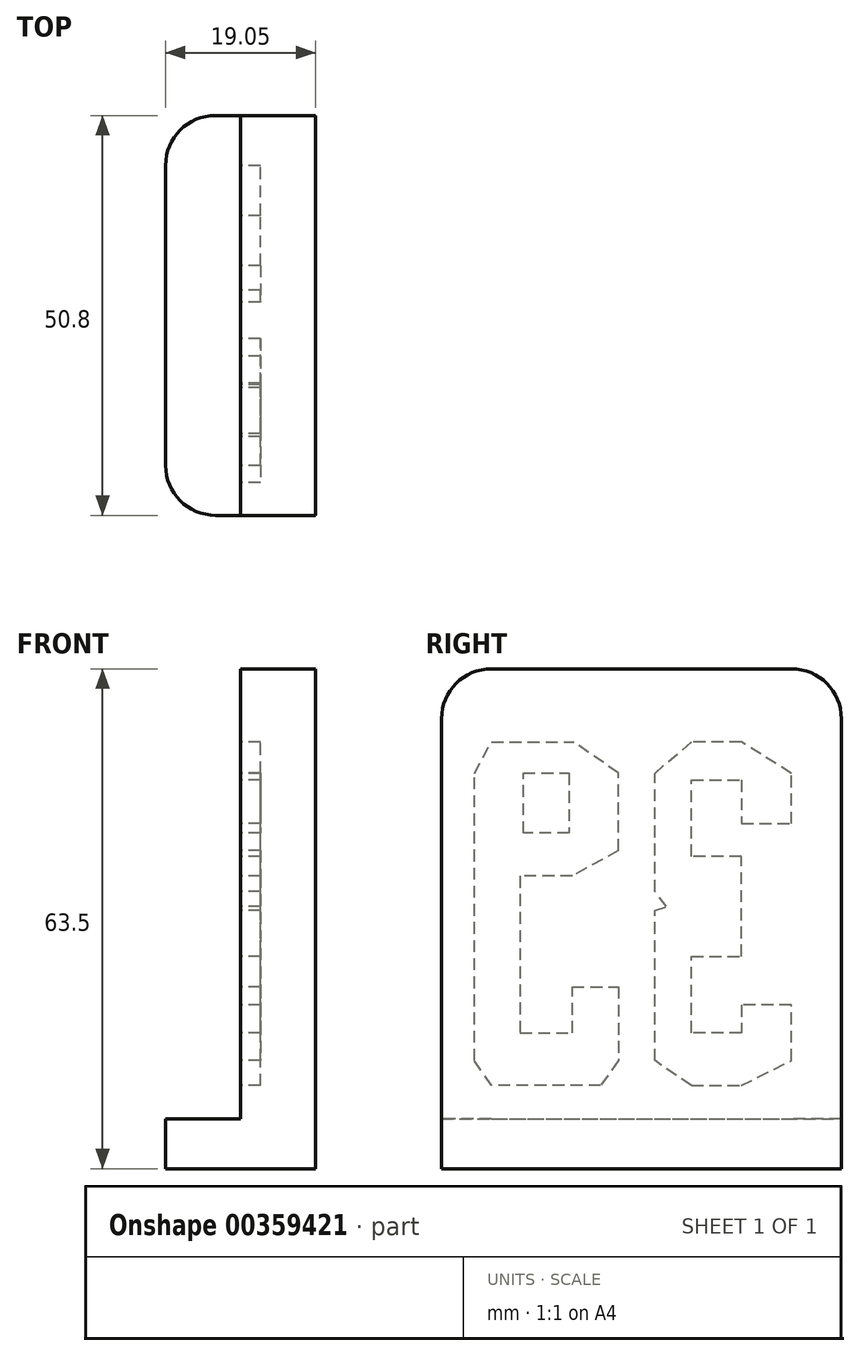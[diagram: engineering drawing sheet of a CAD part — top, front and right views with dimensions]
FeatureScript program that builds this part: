
annotation { "Feature Type Name" : "Feature", "Feature Type Description" : "" }
export const myFeature = defineFeature(function(context is Context, id is Id, definition is map)
    precondition{}
    {
        {
            var Q0;
            Q0=qCreatedBy(makeId("Front.planeOp"),FACE);
            var sketch = newSketch(context, id + "F0", { "sketchPlane" : qUnion([Q0])});
            skLineSegment(sketch, "E0", {"start": v(0, 0) * mm, "end": v(0, 6.35) * mm});
            skLineSegment(sketch, "E1", {"start": v(0, 6.35) * mm, "end": v(9.53, 6.35) * mm});
            skLineSegment(sketch, "E2", {"start": v(9.53, 6.35) * mm, "end": v(9.52, 63.5) * mm});
            skLineSegment(sketch, "E3", {"start": v(9.52, 63.5) * mm, "end": v(19.05, 63.5) * mm});
            skLineSegment(sketch, "E4", {"start": v(19.05, 63.5) * mm, "end": v(19.05, 0) * mm});
            skLineSegment(sketch, "E5", {"start": v(19.05, 0) * mm, "end": v(0, 0) * mm});
            skSolve(sketch);
        }
        {
            var Q0;
            Q0=makeQuery(id+"F0.imprint","IMPRINT",FACE,{"disambiguationData":[TD([[makeQuery(id+"F0.imprint","IMPRINT",EDGE,{"derivedFrom":sQuery(id+"F0.wireOp",EDGE,"E0")}),-1.0]])]});
            extrude(context, id + "F1", {"entities" : qUnion([Q0]), "depth" : 50.8 * mm});
        }
        {
            var Q0;
            Q0=makeQuery(id+"F1.opExtrude","SWEPT_FACE",FACE,{"disambiguationData":[OSD([sQuery(id+"F0.wireOp",EDGE,"E1")])]});
            var sketch = newSketch(context, id + "F2", { "sketchPlane" : qUnion([Q0])});
            skLineSegment(sketch, "E6", {"start": v(9.53, 0) * mm, "end": v(6.35, 0) * mm});
            skLineSegment(sketch, "E7", {"start": v(0, -6.35) * mm, "end": v(0, -44.45) * mm});
            skLineSegment(sketch, "E8", {"start": v(6.35, -50.8) * mm, "end": v(9.53, -50.8) * mm});
            skLineSegment(sketch, "E9", {"start": v(9.53, -50.8) * mm, "end": v(9.53, 0) * mm});
            skPoint(sketch, "E10.visualSharp", {"position": v(0, 0) * mm});
            skArc(sketch, "E10.filletArc", {"start": v(6.35, 0) * mm, "mid": v(1.86, -1.86) * mm, "end": v(0, -6.35) * mm});
            skPoint(sketch, "E11.visualSharp", {"position": v(0, -50.8) * mm});
            skArc(sketch, "E11.filletArc", {"start": v(0, -44.45) * mm, "mid": v(1.86, -48.94) * mm, "end": v(6.35, -50.8) * mm});
            skSolve(sketch);
        }
        {
            var Q0;
            {var subQ0=sQuery(id+"F2.wireOp",EDGE,"E10.filletArc");Q0=makeQuery(id+"F2.imprint","IMPRINT",FACE,{"disambiguationData":[TD([[makeQuery(id+"F2.imprint","IMPRINT",EDGE,{"derivedFrom":subQ0}),-1.0]])]});}
            var Q1;
            {var subQ0=sQuery(id+"F2.wireOp",EDGE,"E11.filletArc");Q1=makeQuery(id+"F2.imprint","IMPRINT",FACE,{"disambiguationData":[TD([[makeQuery(id+"F2.imprint","IMPRINT",EDGE,{"derivedFrom":subQ0}),-1.0]])]});}
            extrude(context, id + "F3", {"entities" : qUnion([Q0, Q1]), "operationType" : NewBodyOperationType.REMOVE, "oppositeDirection" : true, "depth" : 25.4 * mm});
        }
        {
            var Q0;
            Q0=makeQuery(id+"F1.opExtrude","SWEPT_FACE",FACE,{"disambiguationData":[OSD([sQuery(id+"F0.wireOp",EDGE,"E2")])]});
            var sketch = newSketch(context, id + "F4", { "sketchPlane" : qUnion([Q0])});
            skLineSegment(sketch, "E12", {"start": v(50.8, 57.15) * mm, "end": v(50.8, 6.35) * mm});
            skLineSegment(sketch, "E13", {"start": v(50.8, 6.35) * mm, "end": v(0, 6.35) * mm});
            skLineSegment(sketch, "E14", {"start": v(0, 6.35) * mm, "end": v(0, 57.15) * mm});
            skLineSegment(sketch, "E15", {"start": v(6.35, 63.5) * mm, "end": v(44.45, 63.5) * mm});
            skPoint(sketch, "E16.visualSharp", {"position": v(0, 63.5) * mm});
            skArc(sketch, "E16.filletArc", {"start": v(6.35, 63.5) * mm, "mid": v(1.86, 61.64) * mm, "end": v(0, 57.15) * mm});
            skPoint(sketch, "E17.visualSharp", {"position": v(50.8, 63.5) * mm});
            skArc(sketch, "E17.filletArc", {"start": v(50.8, 57.15) * mm, "mid": v(48.94, 61.64) * mm, "end": v(44.45, 63.5) * mm});
            skSolve(sketch);
        }
        {
            var Q0;
            {var subQ0=sQuery(id+"F4.wireOp",EDGE,"E16.filletArc");Q0=makeQuery(id+"F4.imprint","IMPRINT",FACE,{"disambiguationData":[TD([[makeQuery(id+"F4.imprint","IMPRINT",EDGE,{"derivedFrom":subQ0}),-1.0]])]});}
            var Q1;
            {var subQ0=sQuery(id+"F4.wireOp",EDGE,"E17.filletArc");Q1=makeQuery(id+"F4.imprint","IMPRINT",FACE,{"disambiguationData":[TD([[makeQuery(id+"F4.imprint","IMPRINT",EDGE,{"derivedFrom":subQ0}),-1.0]])]});}
            var Q2;
            Q2=sQuery(id+"F4.wireOp",EDGE,"E12");
            var Q3;
            Q3=sQuery(id+"F4.wireOp",EDGE,"E13");
            var Q4;
            Q4=sQuery(id+"F4.wireOp",EDGE,"E14");
            var Q5;
            Q5=sQuery(id+"F4.wireOp",EDGE,"E15");
            var Q6;
            Q6=sQuery(id+"F4.wireOp",EDGE,"E17.filletArc");
            extrude(context, id + "F5", {"entities" : qUnion([Q0, Q1]), "operationType" : NewBodyOperationType.REMOVE, "surfaceEntities" : qUnion([Q2, Q3, Q4, Q5, Q6]), "oppositeDirection" : true, "depth" : 25.4 * mm});
        }
        {
            var Q0;
            Q0=makeQuery(id+"F1.opExtrude","SWEPT_FACE",FACE,{"disambiguationData":[OSD([sQuery(id+"F0.wireOp",EDGE,"E2")])]});
            var sketch = newSketch(context, id + "F6", { "sketchPlane" : qUnion([Q0])});
            skLineSegment(sketch, "E18", {"start": v(6.35, 43.84) * mm, "end": v(6.35, 50.22) * mm});
            skLineSegment(sketch, "E19", {"start": v(6.35, 50.22) * mm, "end": v(12.7, 54.2) * mm});
            skLineSegment(sketch, "E20", {"start": v(12.7, 54.2) * mm, "end": v(19.05, 54.2) * mm});
            skLineSegment(sketch, "E21", {"start": v(19.05, 10.57) * mm, "end": v(12.7, 10.57) * mm});
            skLineSegment(sketch, "E22", {"start": v(12.7, 10.57) * mm, "end": v(6.35, 13.73) * mm});
            skLineSegment(sketch, "E23", {"start": v(6.35, 13.73) * mm, "end": v(6.35, 20.8) * mm});
            skLineSegment(sketch, "E24", {"start": v(6.35, 20.8) * mm, "end": v(12.7, 20.8) * mm});
            skLineSegment(sketch, "E25", {"start": v(12.7, 20.8) * mm, "end": v(12.7, 17.26) * mm});
            skPoint(sketch, "E25.endSnap0", {"position": v(6.35, 17.26) * mm});
            skLineSegment(sketch, "E26", {"start": v(12.7, 17.26) * mm, "end": v(19.05, 17.26) * mm});
            skLineSegment(sketch, "E27", {"start": v(19.05, 17.26) * mm, "end": v(19.05, 26.96) * mm});
            skLineSegment(sketch, "E28", {"start": v(19.05, 26.96) * mm, "end": v(12.7, 26.96) * mm});
            skLineSegment(sketch, "E29", {"start": v(12.7, 26.96) * mm, "end": v(12.7, 39.66) * mm});
            skLineSegment(sketch, "E30", {"start": v(12.7, 39.66) * mm, "end": v(19.05, 39.66) * mm});
            skLineSegment(sketch, "E31", {"start": v(19.05, 39.66) * mm, "end": v(19.05, 49.35) * mm});
            skLineSegment(sketch, "E32", {"start": v(19.05, 49.35) * mm, "end": v(12.7, 49.35) * mm});
            skLineSegment(sketch, "E33", {"start": v(12.7, 49.35) * mm, "end": v(12.7, 43.84) * mm});
            skLineSegment(sketch, "E34", {"start": v(12.7, 43.84) * mm, "end": v(6.35, 43.84) * mm});
            skPoint(sketch, "E35.endSnap0", {"position": v(12.7, 33.3) * mm});
            skLineSegment(sketch, "E36", {"start": v(19.05, 10.57) * mm, "end": v(23.71, 13.73) * mm});
            skLineSegment(sketch, "E37", {"start": v(23.71, 13.73) * mm, "end": v(23.71, 32.78) * mm});
            skLineSegment(sketch, "E38", {"start": v(23.71, 32.78) * mm, "end": v(22.2, 33.3) * mm});
            skLineSegment(sketch, "E39", {"start": v(22.2, 33.3) * mm, "end": v(23.71, 35.2) * mm});
            skLineSegment(sketch, "E40", {"start": v(23.71, 35.2) * mm, "end": v(23.71, 50.22) * mm});
            skLineSegment(sketch, "E41", {"start": v(23.71, 50.22) * mm, "end": v(19.05, 54.2) * mm});
            skSolve(sketch);
        }
        {
            var Q0;
            Q0 = qSketchRegion(id + "F6", true);
            extrude(context, id + "F7", {"entities" : qUnion([Q0]), "operationType" : NewBodyOperationType.REMOVE, "oppositeDirection" : true, "depth" : 2.54 * mm});
        }
        {
            var Q0;
            Q0=makeQuery(id+"F1.opExtrude","SWEPT_FACE",FACE,{"disambiguationData":[OSD([sQuery(id+"F0.wireOp",EDGE,"E2")])]});
            var sketch = newSketch(context, id + "F8", { "sketchPlane" : qUnion([Q0])});
            skPoint(sketch, "E42.startSnap0", {"position": v(15.88, 54.2) * mm});
            skLineSegment(sketch, "E43", {"start": v(34.18, 37.2) * mm, "end": v(40.8, 37.2) * mm});
            skLineSegment(sketch, "E44", {"start": v(40.8, 37.2) * mm, "end": v(40.8, 17.26) * mm});
            skLineSegment(sketch, "E45", {"start": v(40.8, 17.26) * mm, "end": v(34.18, 17.26) * mm});
            skLineSegment(sketch, "E46", {"start": v(34.18, 17.26) * mm, "end": v(34.18, 23.12) * mm});
            skLineSegment(sketch, "E47", {"start": v(34.18, 23.12) * mm, "end": v(28.35, 23.12) * mm});
            skLineSegment(sketch, "E48", {"start": v(28.35, 23.12) * mm, "end": v(28.35, 13.73) * mm});
            skLineSegment(sketch, "E49", {"start": v(28.35, 13.73) * mm, "end": v(30.6, 10.57) * mm});
            skLineSegment(sketch, "E50", {"start": v(30.6, 10.57) * mm, "end": v(44.45, 10.57) * mm});
            skLineSegment(sketch, "E51", {"start": v(44.45, 10.57) * mm, "end": v(46.64, 13.73) * mm});
            skLineSegment(sketch, "E52", {"start": v(46.64, 13.73) * mm, "end": v(46.64, 50.22) * mm});
            skLineSegment(sketch, "E53", {"start": v(46.64, 50.22) * mm, "end": v(44.45, 54.2) * mm});
            skLineSegment(sketch, "E54", {"start": v(44.45, 54.2) * mm, "end": v(33.97, 54.2) * mm});
            skLineSegment(sketch, "E55", {"start": v(28.35, 40.4) * mm, "end": v(28.35, 50.26) * mm});
            skLineSegment(sketch, "E56", {"start": v(28.35, 50.26) * mm, "end": v(33.97, 54.2) * mm});
            skLineSegment(sketch, "E57", {"start": v(28.35, 40.4) * mm, "end": v(34.18, 37.2) * mm});
            skLineSegment(sketch, "E58", {"start": v(34.58, 50.26) * mm, "end": v(34.58, 42.62) * mm});
            skLineSegment(sketch, "E59", {"start": v(34.58, 42.62) * mm, "end": v(40.4, 42.62) * mm});
            skLineSegment(sketch, "E60", {"start": v(40.4, 42.62) * mm, "end": v(40.4, 50.26) * mm});
            skLineSegment(sketch, "E61", {"start": v(40.4, 50.26) * mm, "end": v(34.58, 50.26) * mm});
            skSolve(sketch);
        }
        {
            var Q0;
            Q0=makeQuery(id+"F8.imprint","IMPRINT",FACE,{"disambiguationData":[TD([[makeQuery(id+"F8.imprint","IMPRINT",EDGE,{"derivedFrom":sQuery(id+"F8.wireOp",EDGE,"E43")}),1.0]])]});
            extrude(context, id + "F9", {"entities" : qUnion([Q0]), "operationType" : NewBodyOperationType.REMOVE, "oppositeDirection" : true, "depth" : 2.54 * mm});
        }
    });
